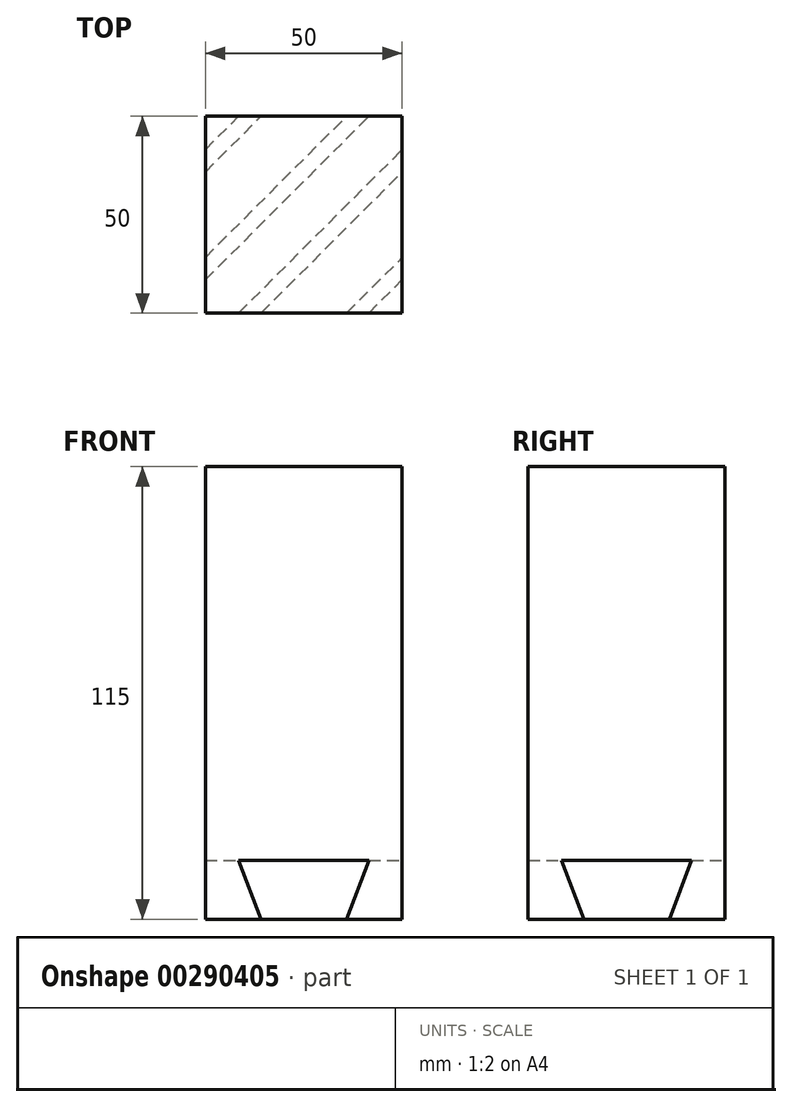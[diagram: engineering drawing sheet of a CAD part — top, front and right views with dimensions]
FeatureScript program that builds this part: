
annotation { "Feature Type Name" : "Feature", "Feature Type Description" : "" }
export const myFeature = defineFeature(function(context is Context, id is Id, definition is map)
    precondition{}
    {
        {
            var Q0;
            Q0=qCreatedBy(makeId("Top.planeOp"),FACE);
            var sketch = newSketch(context, id + "F0", { "sketchPlane" : qUnion([Q0])});
            skLineSegment(sketch, "E0.bottom", {"start": v(25, 25) * mm, "end": v(-25, 25) * mm});
            skLineSegment(sketch, "E0.top", {"start": v(25, -25) * mm, "end": v(-25, -25) * mm});
            skLineSegment(sketch, "E0.left", {"start": v(25, 25) * mm, "end": v(25, -25) * mm});
            skLineSegment(sketch, "E0.right", {"start": v(-25, 25) * mm, "end": v(-25, -25) * mm});
            skPoint(sketch, "E0.middle", {"position": v(0, 0) * mm});
            skSolve(sketch);
        }
        {
            var Q0;
            Q0 = qSketchRegion(id + "F0", true);
            extrude(context, id + "F1", {"entities" : qUnion([Q0]), "depth" : 100 * mm});
        }
        {
            var Q0;
            Q0=makeQuery(id+"F1.opExtrude","CAP_VERTEX",VERTEX,{"disambiguationData":[OSD([sQuery(id+"F0.wireOp",EDGE,"E0.bottom"),sQuery(id+"F0.wireOp",EDGE,"E0.right")])],"isStart":false});
            var Q1;
            Q1=makeQuery(id+"F1.opExtrude","CAP_VERTEX",VERTEX,{"disambiguationData":[OSD([sQuery(id+"F0.wireOp",EDGE,"E0.top"),sQuery(id+"F0.wireOp",EDGE,"E0.left")])],"isStart":false});
            var Q2;
            Q2=makeQuery(id+"F1.opExtrude","CAP_VERTEX",VERTEX,{"disambiguationData":[OSD([sQuery(id+"F0.wireOp",EDGE,"E0.top"),sQuery(id+"F0.wireOp",EDGE,"E0.left")])],"isStart":true});
            cPlane(context, id + "F2", {"entities" : qUnion([Q0, Q1, Q2]), "cplaneType" : CPlaneType.THREE_POINT, "offset" : 25 * mm, "width" : 150 * mm, "height" : 150 * mm});
        }
        {
            var Q0;
            Q0=qCreatedBy(id+"F2.planeOp",FACE);
            var sketch = newSketch(context, id + "F3", { "sketchPlane" : qUnion([Q0])});
            skLineSegment(sketch, "E1", {"start": v(0, 0) * mm, "end": v(0, -15) * mm, "construction": true});
            skLineSegment(sketch, "E2", {"start": v(-35.36, 0) * mm, "end": v(-35.36, -15) * mm});
            skLineSegment(sketch, "E3", {"start": v(35.36, 0) * mm, "end": v(35.36, -15) * mm});
            skLineSegment(sketch, "E4", {"start": v(-5.98, 0) * mm, "end": v(5.98, 0) * mm});
            skLineSegment(sketch, "E5", {"start": v(5.98, 0) * mm, "end": v(10, -15) * mm});
            skLineSegment(sketch, "E6", {"start": v(10, -15) * mm, "end": v(-10, -15) * mm});
            skLineSegment(sketch, "E7", {"start": v(-10, -15) * mm, "end": v(-5.98, 0) * mm});
            skLineSegment(sketch, "E8", {"start": v(35.36, 0) * mm, "end": v(29.37, 0) * mm});
            skLineSegment(sketch, "E9", {"start": v(29.37, 0) * mm, "end": v(25.36, -15) * mm});
            skLineSegment(sketch, "E10", {"start": v(25.36, -15) * mm, "end": v(35.36, -15) * mm});
            skLineSegment(sketch, "E11", {"start": v(-35.36, 0) * mm, "end": v(-29.37, 0) * mm});
            skLineSegment(sketch, "E12", {"start": v(-29.37, 0) * mm, "end": v(-25.36, -15) * mm});
            skLineSegment(sketch, "E13", {"start": v(-25.36, -15) * mm, "end": v(-35.36, -15) * mm});
            skSolve(sketch);
        }
        {
            var Q0;
            Q0 = qSketchRegion(id + "F3", true);
            var Q1;
            Q1=makeQuery(id+"F1.opExtrude","SWEPT_FACE",FACE,{"disambiguationData":[OSD([sQuery(id+"F0.wireOp",EDGE,"E0.right")])]});
            var Q2;
            Q2=makeQuery(id+"F1.opExtrude","SWEPT_FACE",FACE,{"disambiguationData":[OSD([sQuery(id+"F0.wireOp",EDGE,"E0.top")])]});
            extrude(context, id + "F4", {"entities" : qUnion([Q0]), "operationType" : NewBodyOperationType.ADD, "endBound" : BoundingType.SYMMETRIC, "endBoundEntityFace" : qUnion([Q1]), "depth" : 100 * mm});
        }
        {
            var Q0;
            {var subQ0=sQuery(id+"F0.wireOp",EDGE,"E0.left");var subQ1=sQuery(id+"F0.wireOp",EDGE,"E0.top");Q0=makeQuery(id+"F4.boolean.opBoolean","SPLIT",FACE,{"disambiguationData":[TD([makeQuery(id+"F1.opExtrude","SWEPT_FACE",FACE,{"disambiguationData":[OSD([subQ1])]})])],"derivedFrom":makeQuery(id+"F1.opExtrude","CAP_FACE",FACE,{"disambiguationData":[OSD([sQuery(id+"F0.wireOp",EDGE,"E0.bottom"),subQ1,subQ0,sQuery(id+"F0.wireOp",EDGE,"E0.right")])],"isStart":true})});}
            var sketch = newSketch(context, id + "F5", { "sketchPlane" : qUnion([Q0])});
            skLineSegment(sketch, "E14.0.0", {"start": v(-25, 25) * mm, "end": v(25, 25) * mm});
            skLineSegment(sketch, "E14.0.1", {"start": v(25, 25) * mm, "end": v(25, -25) * mm});
            skLineSegment(sketch, "E14.0.2", {"start": v(25, -25) * mm, "end": v(-25, -25) * mm});
            skLineSegment(sketch, "E14.0.3", {"start": v(-25, -25) * mm, "end": v(-25, 25) * mm});
            skLineSegment(sketch, "E15.0", {"start": v(75, 75) * mm, "end": v(75, -75) * mm});
            skLineSegment(sketch, "E15.1", {"start": v(-75, 75) * mm, "end": v(75, 75) * mm});
            skLineSegment(sketch, "E15.2", {"start": v(-75, -75) * mm, "end": v(-75, 75) * mm});
            skLineSegment(sketch, "E15.3", {"start": v(75, -75) * mm, "end": v(-75, -75) * mm});
            skSolve(sketch);
        }
        {
            var Q0;
            Q0 = qSketchRegion(id + "F5", true);
            var Q1;
            Q1=makeQuery(id+"F4.opExtrude","SWEPT_FACE",FACE,{"disambiguationData":[OSD([sQuery(id+"F3.wireOp",EDGE,"E6")])]});
            extrude(context, id + "F6", {"entities" : qUnion([Q0]), "operationType" : NewBodyOperationType.REMOVE, "endBound" : BoundingType.UP_TO_SURFACE, "endBoundEntityFace" : qUnion([Q1]), "depth" : 25 * mm});
        }
    });
